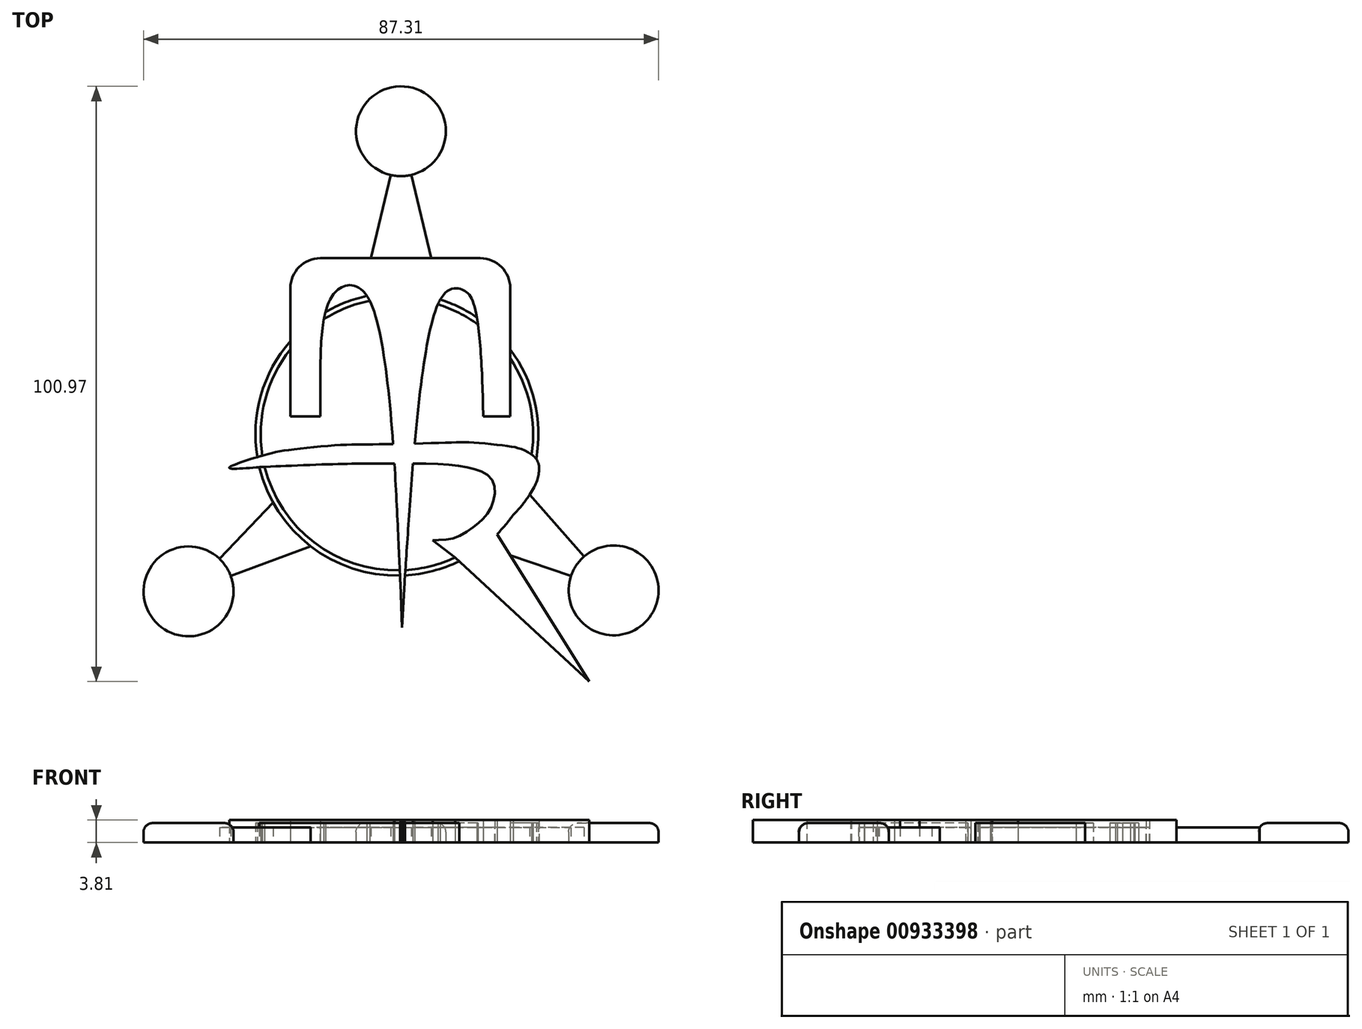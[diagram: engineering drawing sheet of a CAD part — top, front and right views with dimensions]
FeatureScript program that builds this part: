
annotation { "Feature Type Name" : "Feature", "Feature Type Description" : "" }
export const myFeature = defineFeature(function(context is Context, id is Id, definition is map)
    precondition{}
    {
        {
            var Q0;
            Q0=qCreatedBy(makeId("Top.planeOp"),FACE);
            var sketch = newSketch(context, id + "F0", { "sketchPlane" : qUnion([Q0])});
            skCircle(sketch, "E0", {"center": v(-18.12, 70.03) * mm, "radius": 7.62 * mm});
            skCircle(sketch, "E1", {"center": v(17.93, -7.86) * mm, "radius": 7.62 * mm});
            skCircle(sketch, "E2", {"center": v(-54.14, -8.03) * mm, "radius": 7.62 * mm});
            skCircle(sketch, "E3", {"center": v(-18.8, 18.65) * mm, "radius": 23.1 * mm});
            skLineSegment(sketch, "E4", {"start": v(-54.14, -8.03) * mm, "end": v(-39.17, 7.74) * mm});
            skLineSegment(sketch, "E5", {"start": v(-54.14, -8.03) * mm, "end": v(-32.45, 0) * mm});
            skLineSegment(sketch, "E6", {"start": v(-5.15, 0) * mm, "end": v(17.93, -7.86) * mm});
            skLineSegment(sketch, "E7", {"start": v(17.93, -7.86) * mm, "end": v(2.4, 9.9) * mm});
            skLineSegment(sketch, "E8", {"start": v(-18.12, 70.03) * mm, "end": v(-28.3, 26.96) * mm});
            skLineSegment(sketch, "E9", {"start": v(-18.12, 70.03) * mm, "end": v(-11.05, 40.42) * mm});
            skPoint(sketch, "E10.startSnap0", {"position": v(-23.2, 48.5) * mm});
            skLineSegment(sketch, "E11", {"start": v(-36.87, 21.63) * mm, "end": v(-36.87, 48.5) * mm});
            skLineSegment(sketch, "E12", {"start": v(0.4, 21.63) * mm, "end": v(0.4, 48.5) * mm});
            skFitSpline(sketch, "E13", {"points": [v(-31.8, 21.63) * mm, v(-30.76, 39.94) * mm, v(-28.08, 43.6) * mm, v(-23.14, 40.68) * mm, v(-17.9, -9.73) * mm, v(-11.9, 40.58) * mm, v(-7.9, 43.22) * mm, v(-5.88, 41.03) * mm, v(-4.16, 21.63) * mm], "startDerivative": vector(-1.17, 195.1) * mm, "endDerivative": vector(3.47, -161.5) * mm});
            skLineSegment(sketch, "E14", {"start": v(-36.87, 48.5) * mm, "end": v(0.4, 48.5) * mm});
            skLineSegment(sketch, "E15", {"start": v(-17.9, -9.73) * mm, "end": v(-17.9, -14.17) * mm});
            skLineSegment(sketch, "E16", {"start": v(-17.9, -14.17) * mm, "end": v(-17.52, -6.55) * mm});
            skLineSegment(sketch, "E17", {"start": v(-17.52, -6.55) * mm, "end": v(-18.21, -6.73) * mm});
            skLineSegment(sketch, "E18", {"start": v(-18.21, -6.73) * mm, "end": v(-17.9, -14.17) * mm});
            skLineSegment(sketch, "E19", {"start": v(-36.87, 21.63) * mm, "end": v(-31.8, 21.63) * mm});
            skLineSegment(sketch, "E20", {"start": v(-4.16, 21.63) * mm, "end": v(0.4, 21.63) * mm});
            skLineSegment(sketch, "E21", {"start": v(2.4, 9.9) * mm, "end": v(1.54, 10.88) * mm});
            skLineSegment(sketch, "E22", {"start": v(-2.32, 2.44) * mm, "end": v(13.81, -23.32) * mm});
            skLineSegment(sketch, "E23", {"start": v(13.81, -23.32) * mm, "end": v(-8.94, -2.26) * mm});
            skLineSegment(sketch, "E24", {"start": v(-8.94, -2.26) * mm, "end": v(-12.76, 0.66) * mm});
            skFitSpline(sketch, "E25", {"points": [v(-2.32, 2.44) * mm, v(0, 4.2) * mm, v(1.94, 6) * mm, v(4.56, 9.84) * mm, v(5.3, 12.42) * mm, v(4.8, 14.47) * mm, v(2.43, 16.06) * mm, v(0, 16.62) * mm, v(-5.95, 17.23) * mm, v(-10.01, 17.21) * mm, v(-21.72, 16.93) * mm, v(-28.25, 16.82) * mm, v(-37.37, 15.94) * mm, v(-41.62, 15.02) * mm, v(-47.23, 12.94) * mm, v(-42.13, 13.05) * mm, v(-38.06, 13.23) * mm, v(-33.34, 13.44) * mm, v(-29.13, 13.56) * mm, v(-26.22, 13.64) * mm, v(-22.13, 13.65) * mm, v(-14.68, 13.65) * mm, v(-8.81, 13.33) * mm, v(-5.68, 12.71) * mm, v(-3.59, 11.87) * mm, v(-2.32, 10.15) * mm, v(-2.32, 7.85) * mm, v(-3.15, 5.58) * mm, v(-4.58, 3.91) * mm, v(-5.97, 2.8) * mm, v(-8.54, 1.23) * mm, v(-10.7, 0.74) * mm, v(-12.76, 0.66) * mm], "startDerivative": vector(96.56, 70.7) * mm, "endDerivative": vector(-65.55, -2.96) * mm});
            skCircle(sketch, "E26", {"center": v(-18.8, 18.65) * mm, "radius": 24 * mm});
            skSolve(sketch);
        }
        {
            var Q0;
            {var subQ0=sQuery(id+"F0.wireOp",EDGE,"E14");var subQ3=sQuery(id+"F0.wireOp",EDGE,"E8");var subQ4=makeQuery(id+"F0.imprint","INTERSECT",VERTEX,{"derivedFrom":[subQ3,subQ0]});Q0=makeQuery(id+"F0.imprint","IMPRINT",FACE,{"disambiguationData":[TD([[makeQuery(id+"F0.imprint","IMPRINT",EDGE,{"disambiguationData":[TD([[subQ4,-1.0]])],"derivedFrom":subQ3}),-1.0]])]});}
            var Q1;
            {var subQ0=sQuery(id+"F0.wireOp",EDGE,"E13");var subQ1=sQuery(id+"F0.wireOp",EDGE,"E3");var subQ2=makeQuery(id+"F0.imprint","INTERSECT",VERTEX,{"disambiguationData":[OD(3.0)],"derivedFrom":[subQ1,subQ0]});Q1=makeQuery(id+"F0.imprint","IMPRINT",FACE,{"disambiguationData":[TD([[makeQuery(id+"F0.imprint","IMPRINT",EDGE,{"disambiguationData":[TD([[subQ2,-1.0]])],"derivedFrom":subQ1}),-1.0]])]});}
            var Q2;
            {var subQ5=sQuery(id+"F0.wireOp",EDGE,"E19");Q2=makeQuery(id+"F0.imprint","IMPRINT",FACE,{"disambiguationData":[TD([[makeQuery(id+"F0.imprint","IMPRINT",EDGE,{"derivedFrom":subQ5}),1.0]])]});}
            var Q3;
            {var subQ5=sQuery(id+"F0.wireOp",EDGE,"E8");var subQ8=sQuery(id+"F0.wireOp",EDGE,"E14");var subQ10=makeQuery(id+"F0.imprint","INTERSECT",VERTEX,{"derivedFrom":[subQ5,subQ8]});Q3=makeQuery(id+"F0.imprint","IMPRINT",FACE,{"disambiguationData":[TD([[makeQuery(id+"F0.imprint","IMPRINT",EDGE,{"disambiguationData":[TD([[subQ10,-1.0]])],"derivedFrom":subQ5}),1.0]])]});}
            var Q4;
            {var subQ0=sQuery(id+"F0.wireOp",EDGE,"E14");var subQ3=sQuery(id+"F0.wireOp",EDGE,"E9");var subQ4=makeQuery(id+"F0.imprint","INTERSECT",VERTEX,{"derivedFrom":[subQ3,subQ0]});Q4=makeQuery(id+"F0.imprint","IMPRINT",FACE,{"disambiguationData":[TD([[makeQuery(id+"F0.imprint","IMPRINT",EDGE,{"disambiguationData":[TD([[subQ4,-1.0]])],"derivedFrom":subQ3}),1.0]])]});}
            var Q5;
            {var subQ0=sQuery(id+"F0.wireOp",EDGE,"E13");var subQ1=sQuery(id+"F0.wireOp",EDGE,"E3");var subQ2=makeQuery(id+"F0.imprint","INTERSECT",VERTEX,{"disambiguationData":[OD(1.0)],"derivedFrom":[subQ1,subQ0]});Q5=makeQuery(id+"F0.imprint","IMPRINT",FACE,{"disambiguationData":[TD([[makeQuery(id+"F0.imprint","IMPRINT",EDGE,{"disambiguationData":[TD([[subQ2,-1.0]])],"derivedFrom":subQ1}),1.0]])]});}
            var Q6;
            {var subQ0=sQuery(id+"F0.wireOp",EDGE,"E13");var subQ1=sQuery(id+"F0.wireOp",EDGE,"E3");var subQ2=makeQuery(id+"F0.imprint","INTERSECT",VERTEX,{"disambiguationData":[OD(1.0)],"derivedFrom":[subQ1,subQ0]});Q6=makeQuery(id+"F0.imprint","IMPRINT",FACE,{"disambiguationData":[TD([[makeQuery(id+"F0.imprint","IMPRINT",EDGE,{"disambiguationData":[TD([[subQ2,-1.0]])],"derivedFrom":subQ1}),-1.0]])]});}
            var Q7;
            {var subQ0=sQuery(id+"F0.wireOp",EDGE,"E25");var subQ1=sQuery(id+"F0.wireOp",EDGE,"E3");var subQ2=makeQuery(id+"F0.imprint","INTERSECT",VERTEX,{"disambiguationData":[OD(0.0)],"derivedFrom":[subQ1,subQ0]});Q7=makeQuery(id+"F0.imprint","IMPRINT",FACE,{"disambiguationData":[TD([[makeQuery(id+"F0.imprint","IMPRINT",EDGE,{"disambiguationData":[TD([[subQ2,-1.0]])],"derivedFrom":subQ1}),1.0]])]});}
            var Q8;
            {var subQ0=sQuery(id+"F0.wireOp",EDGE,"E26");var subQ1=sQuery(id+"F0.wireOp",EDGE,"E25");var subQ2=makeQuery(id+"F0.imprint","INTERSECT",VERTEX,{"disambiguationData":[OD(1.0)],"derivedFrom":[subQ1,subQ0]});Q8=makeQuery(id+"F0.imprint","IMPRINT",FACE,{"disambiguationData":[TD([[makeQuery(id+"F0.imprint","IMPRINT",EDGE,{"disambiguationData":[TD([[subQ2,-1.0]])],"derivedFrom":subQ1}),1.0]])]});}
            var Q9;
            {var subQ0=sQuery(id+"F0.wireOp",EDGE,"E25");var subQ1=sQuery(id+"F0.wireOp",EDGE,"E3");var subQ2=makeQuery(id+"F0.imprint","INTERSECT",VERTEX,{"disambiguationData":[OD(0.0)],"derivedFrom":[subQ1,subQ0]});Q9=makeQuery(id+"F0.imprint","IMPRINT",FACE,{"disambiguationData":[TD([[makeQuery(id+"F0.imprint","IMPRINT",EDGE,{"disambiguationData":[TD([[subQ2,-1.0]])],"derivedFrom":subQ1}),-1.0]])]});}
            var Q10;
            {var subQ0=sQuery(id+"F0.wireOp",EDGE,"E25");var subQ1=sQuery(id+"F0.wireOp",EDGE,"E13");var subQ2=makeQuery(id+"F0.imprint","INTERSECT",VERTEX,{"disambiguationData":[OD(0.0)],"derivedFrom":[subQ1,subQ0]});Q10=makeQuery(id+"F0.imprint","IMPRINT",FACE,{"disambiguationData":[TD([[makeQuery(id+"F0.imprint","IMPRINT",EDGE,{"disambiguationData":[TD([[subQ2,-1.0]])],"derivedFrom":subQ1}),1.0]])]});}
            var Q11;
            {var subQ0=sQuery(id+"F0.wireOp",EDGE,"E13");var subQ1=sQuery(id+"F0.wireOp",EDGE,"E3");var subQ2=makeQuery(id+"F0.imprint","INTERSECT",VERTEX,{"disambiguationData":[OD(4.0)],"derivedFrom":[subQ1,subQ0]});Q11=makeQuery(id+"F0.imprint","IMPRINT",FACE,{"disambiguationData":[TD([[makeQuery(id+"F0.imprint","IMPRINT",EDGE,{"disambiguationData":[TD([[subQ2,-1.0]])],"derivedFrom":subQ1}),1.0]])]});}
            var Q12;
            {var subQ6=sQuery(id+"F0.wireOp",EDGE,"E24");Q12=makeQuery(id+"F0.imprint","IMPRINT",FACE,{"disambiguationData":[TD([[makeQuery(id+"F0.imprint","IMPRINT",EDGE,{"derivedFrom":subQ6}),-1.0]])]});}
            var Q13;
            {var subQ0=sQuery(id+"F0.wireOp",EDGE,"E6");var subQ1=sQuery(id+"F0.wireOp",EDGE,"E3");var subQ2=makeQuery(id+"F0.imprint","INTERSECT",VERTEX,{"derivedFrom":[subQ1,subQ0]});Q13=makeQuery(id+"F0.imprint","IMPRINT",FACE,{"disambiguationData":[TD([[makeQuery(id+"F0.imprint","IMPRINT",EDGE,{"disambiguationData":[TD([[subQ2,-1.0]])],"derivedFrom":subQ0}),-1.0]])]});}
            var Q14;
            {var subQ0=sQuery(id+"F0.wireOp",EDGE,"E22");var subQ1=sQuery(id+"F0.wireOp",EDGE,"E6");var subQ2=makeQuery(id+"F0.imprint","INTERSECT",VERTEX,{"derivedFrom":[subQ1,subQ0]});Q14=makeQuery(id+"F0.imprint","IMPRINT",FACE,{"disambiguationData":[TD([[makeQuery(id+"F0.imprint","IMPRINT",EDGE,{"disambiguationData":[TD([[subQ2,1.0]])],"derivedFrom":subQ1}),-1.0]])]});}
            var Q15;
            {var subQ0=sQuery(id+"F0.wireOp",EDGE,"E6");var subQ1=sQuery(id+"F0.wireOp",EDGE,"E3");var subQ2=makeQuery(id+"F0.imprint","INTERSECT",VERTEX,{"derivedFrom":[subQ1,subQ0]});Q15=makeQuery(id+"F0.imprint","IMPRINT",FACE,{"disambiguationData":[TD([[makeQuery(id+"F0.imprint","IMPRINT",EDGE,{"disambiguationData":[TD([[subQ2,-1.0]])],"derivedFrom":subQ0}),1.0]])]});}
            var Q16;
            {var subQ0=sQuery(id+"F0.wireOp",EDGE,"E22");var subQ1=sQuery(id+"F0.wireOp",EDGE,"E6");var subQ2=makeQuery(id+"F0.imprint","INTERSECT",VERTEX,{"derivedFrom":[subQ1,subQ0]});Q16=makeQuery(id+"F0.imprint","IMPRINT",FACE,{"disambiguationData":[TD([[makeQuery(id+"F0.imprint","IMPRINT",EDGE,{"disambiguationData":[TD([[subQ2,1.0]])],"derivedFrom":subQ1}),1.0]])]});}
            var Q17;
            {var subQ0=sQuery(id+"F0.wireOp",EDGE,"E7");var subQ1=sQuery(id+"F0.wireOp",EDGE,"E3");var subQ2=makeQuery(id+"F0.imprint","INTERSECT",VERTEX,{"derivedFrom":[subQ1,subQ0]});Q17=makeQuery(id+"F0.imprint","IMPRINT",FACE,{"disambiguationData":[TD([[makeQuery(id+"F0.imprint","IMPRINT",EDGE,{"disambiguationData":[TD([[subQ2,-1.0]])],"derivedFrom":subQ1}),-1.0]])]});}
            var Q18;
            {var subQ0=sQuery(id+"F0.wireOp",EDGE,"E25");var subQ1=sQuery(id+"F0.wireOp",EDGE,"E7");var subQ2=makeQuery(id+"F0.imprint","INTERSECT",VERTEX,{"derivedFrom":[subQ1,subQ0]});Q18=makeQuery(id+"F0.imprint","IMPRINT",FACE,{"disambiguationData":[TD([[makeQuery(id+"F0.imprint","IMPRINT",EDGE,{"disambiguationData":[TD([[subQ2,-1.0]])],"derivedFrom":subQ1}),-1.0]])]});}
            var Q19;
            {var subQ0=sQuery(id+"F0.wireOp",EDGE,"E25");var subQ1=sQuery(id+"F0.wireOp",EDGE,"E7");var subQ2=makeQuery(id+"F0.imprint","INTERSECT",VERTEX,{"derivedFrom":[subQ1,subQ0]});Q19=makeQuery(id+"F0.imprint","IMPRINT",FACE,{"disambiguationData":[TD([[makeQuery(id+"F0.imprint","IMPRINT",EDGE,{"disambiguationData":[TD([[subQ2,-1.0]])],"derivedFrom":subQ1}),1.0]])]});}
            var Q20;
            {var subQ1=sQuery(id+"F0.wireOp",EDGE,"E3");var subQ3=sQuery(id+"F0.wireOp",EDGE,"E7");var subQ4=makeQuery(id+"F0.imprint","INTERSECT",VERTEX,{"derivedFrom":[subQ1,subQ3]});Q20=makeQuery(id+"F0.imprint","IMPRINT",FACE,{"disambiguationData":[TD([[makeQuery(id+"F0.imprint","IMPRINT",EDGE,{"disambiguationData":[TD([[subQ4,1.0]])],"derivedFrom":subQ3}),1.0]])]});}
            var Q21;
            {var subQ1=sQuery(id+"F0.wireOp",EDGE,"E22");var subQ3=sQuery(id+"F0.wireOp",EDGE,"E26");var subQ4=makeQuery(id+"F0.imprint","INTERSECT",VERTEX,{"derivedFrom":[subQ1,subQ3]});Q21=makeQuery(id+"F0.imprint","IMPRINT",FACE,{"disambiguationData":[TD([[makeQuery(id+"F0.imprint","IMPRINT",EDGE,{"disambiguationData":[TD([[subQ4,-1.0]])],"derivedFrom":subQ3}),1.0]])]});}
            var Q22;
            {var subQ0=sQuery(id+"F0.wireOp",EDGE,"E17");Q22=makeQuery(id+"F0.imprint","IMPRINT",FACE,{"disambiguationData":[TD([[makeQuery(id+"F0.imprint","IMPRINT",EDGE,{"derivedFrom":subQ0}),-1.0]])]});}
            var Q23;
            {var subQ0=sQuery(id+"F0.wireOp",EDGE,"E13");var subQ1=sQuery(id+"F0.wireOp",EDGE,"E3");var subQ2=makeQuery(id+"F0.imprint","INTERSECT",VERTEX,{"disambiguationData":[OD(4.0)],"derivedFrom":[subQ1,subQ0]});Q23=makeQuery(id+"F0.imprint","IMPRINT",FACE,{"disambiguationData":[TD([[makeQuery(id+"F0.imprint","IMPRINT",EDGE,{"disambiguationData":[TD([[subQ2,-1.0]])],"derivedFrom":subQ1}),-1.0]])]});}
            var Q24;
            {var subQ2=sQuery(id+"F0.wireOp",EDGE,"E17");Q24=makeQuery(id+"F0.imprint","IMPRINT",FACE,{"disambiguationData":[TD([[makeQuery(id+"F0.imprint","IMPRINT",EDGE,{"derivedFrom":subQ2}),1.0]])]});}
            var Q25;
            {var subQ0=sQuery(id+"F0.wireOp",EDGE,"E15");Q25=makeQuery(id+"F0.imprint","IMPRINT",FACE,{"disambiguationData":[TD([[makeQuery(id+"F0.imprint","IMPRINT",EDGE,{"derivedFrom":subQ0}),1.0]])]});}
            var Q26;
            {var subQ0=sQuery(id+"F0.wireOp",EDGE,"E15");Q26=makeQuery(id+"F0.imprint","IMPRINT",FACE,{"disambiguationData":[TD([[makeQuery(id+"F0.imprint","IMPRINT",EDGE,{"derivedFrom":subQ0}),-1.0]])]});}
            var Q27;
            {var subQ0=sQuery(id+"F0.wireOp",EDGE,"E13");var subQ1=sQuery(id+"F0.wireOp",EDGE,"E3");var subQ2=makeQuery(id+"F0.imprint","INTERSECT",VERTEX,{"disambiguationData":[OD(0.0)],"derivedFrom":[subQ1,subQ0]});Q27=makeQuery(id+"F0.imprint","IMPRINT",FACE,{"disambiguationData":[TD([[makeQuery(id+"F0.imprint","IMPRINT",EDGE,{"disambiguationData":[TD([[subQ2,1.0]])],"derivedFrom":subQ1}),-1.0]])]});}
            var Q28;
            {var subQ5=sQuery(id+"F0.wireOp",EDGE,"E20");Q28=makeQuery(id+"F0.imprint","IMPRINT",FACE,{"disambiguationData":[TD([[makeQuery(id+"F0.imprint","IMPRINT",EDGE,{"derivedFrom":subQ5}),1.0]])]});}
            extrude(context, id + "F1", {"entities" : qUnion([Q0, Q1, Q2, Q3, Q4, Q5, Q6, Q7, Q8, Q9, Q10, Q11, Q12, Q13, Q14, Q15, Q16, Q17, Q18, Q19, Q20, Q21, Q22, Q23, Q24, Q25, Q26, Q27, Q28]), "depth" : 3.8 * mm, "offsetDistance" : 25.4 * mm});
        }
        {
            var Q0;
            {var subQ3=sQuery(id+"F0.wireOp",EDGE,"E13");var subQ5=sQuery(id+"F0.wireOp",EDGE,"E26");var subQ6=makeQuery(id+"F0.imprint","INTERSECT",VERTEX,{"disambiguationData":[OD(1.0)],"derivedFrom":[subQ3,subQ5]});Q0=makeQuery(id+"F0.imprint","IMPRINT",FACE,{"disambiguationData":[TD([[makeQuery(id+"F0.imprint","IMPRINT",EDGE,{"disambiguationData":[TD([[subQ6,-1.0]])],"derivedFrom":subQ3}),-1.0]])]});}
            var Q1;
            {var subQ0=sQuery(id+"F0.wireOp",EDGE,"E5");var subQ1=sQuery(id+"F0.wireOp",EDGE,"E3");var subQ2=makeQuery(id+"F0.imprint","INTERSECT",VERTEX,{"derivedFrom":[subQ1,subQ0]});Q1=makeQuery(id+"F0.imprint","IMPRINT",FACE,{"disambiguationData":[TD([[makeQuery(id+"F0.imprint","IMPRINT",EDGE,{"disambiguationData":[TD([[subQ2,-1.0]])],"derivedFrom":subQ1}),-1.0]])]});}
            var Q2;
            {var subQ0=sQuery(id+"F0.wireOp",EDGE,"E4");var subQ1=sQuery(id+"F0.wireOp",EDGE,"E3");var subQ2=makeQuery(id+"F0.imprint","INTERSECT",VERTEX,{"derivedFrom":[subQ1,subQ0]});Q2=makeQuery(id+"F0.imprint","IMPRINT",FACE,{"disambiguationData":[TD([[makeQuery(id+"F0.imprint","IMPRINT",EDGE,{"disambiguationData":[TD([[subQ2,-1.0]])],"derivedFrom":subQ1}),-1.0]])]});}
            var Q3;
            {var subQ0=sQuery(id+"F0.wireOp",EDGE,"E4");var subQ1=sQuery(id+"F0.wireOp",EDGE,"E3");var subQ2=makeQuery(id+"F0.imprint","INTERSECT",VERTEX,{"derivedFrom":[subQ1,subQ0]});Q3=makeQuery(id+"F0.imprint","IMPRINT",FACE,{"disambiguationData":[TD([[makeQuery(id+"F0.imprint","IMPRINT",EDGE,{"disambiguationData":[TD([[subQ2,1.0]])],"derivedFrom":subQ1}),-1.0]])]});}
            var Q4;
            {var subQ0=sQuery(id+"F0.wireOp",EDGE,"E11");var subQ1=sQuery(id+"F0.wireOp",EDGE,"E3");var subQ2=makeQuery(id+"F0.imprint","INTERSECT",VERTEX,{"derivedFrom":[subQ1,subQ0]});Q4=makeQuery(id+"F0.imprint","IMPRINT",FACE,{"disambiguationData":[TD([[makeQuery(id+"F0.imprint","IMPRINT",EDGE,{"disambiguationData":[TD([[subQ2,-1.0]])],"derivedFrom":subQ1}),-1.0]])]});}
            var Q5;
            {var subQ1=sQuery(id+"F0.wireOp",EDGE,"E22");var subQ3=sQuery(id+"F0.wireOp",EDGE,"E26");var subQ4=makeQuery(id+"F0.imprint","INTERSECT",VERTEX,{"derivedFrom":[subQ1,subQ3]});Q5=makeQuery(id+"F0.imprint","IMPRINT",FACE,{"disambiguationData":[TD([[makeQuery(id+"F0.imprint","IMPRINT",EDGE,{"disambiguationData":[TD([[subQ4,-1.0]])],"derivedFrom":subQ3}),1.0]])]});}
            var Q6;
            {var subQ0=sQuery(id+"F0.wireOp",EDGE,"E12");var subQ1=sQuery(id+"F0.wireOp",EDGE,"E3");var subQ2=makeQuery(id+"F0.imprint","INTERSECT",VERTEX,{"derivedFrom":[subQ1,subQ0]});Q6=makeQuery(id+"F0.imprint","IMPRINT",FACE,{"disambiguationData":[TD([[makeQuery(id+"F0.imprint","IMPRINT",EDGE,{"disambiguationData":[TD([[subQ2,1.0]])],"derivedFrom":subQ1}),-1.0]])]});}
            var Q7;
            {var subQ0=sQuery(id+"F0.wireOp",EDGE,"E9");var subQ1=sQuery(id+"F0.wireOp",EDGE,"E3");var subQ2=makeQuery(id+"F0.imprint","INTERSECT",VERTEX,{"derivedFrom":[subQ1,subQ0]});Q7=makeQuery(id+"F0.imprint","IMPRINT",FACE,{"disambiguationData":[TD([[makeQuery(id+"F0.imprint","IMPRINT",EDGE,{"disambiguationData":[TD([[subQ2,1.0]])],"derivedFrom":subQ1}),-1.0]])]});}
            var Q8;
            {var subQ0=sQuery(id+"F0.wireOp",EDGE,"E9");var subQ1=sQuery(id+"F0.wireOp",EDGE,"E3");var subQ2=makeQuery(id+"F0.imprint","INTERSECT",VERTEX,{"derivedFrom":[subQ1,subQ0]});Q8=makeQuery(id+"F0.imprint","IMPRINT",FACE,{"disambiguationData":[TD([[makeQuery(id+"F0.imprint","IMPRINT",EDGE,{"disambiguationData":[TD([[subQ2,-1.0]])],"derivedFrom":subQ1}),-1.0]])]});}
            var Q9;
            {var subQ0=sQuery(id+"F0.wireOp",EDGE,"E8");var subQ1=sQuery(id+"F0.wireOp",EDGE,"E3");var subQ2=makeQuery(id+"F0.imprint","INTERSECT",VERTEX,{"derivedFrom":[subQ1,subQ0]});Q9=makeQuery(id+"F0.imprint","IMPRINT",FACE,{"disambiguationData":[TD([[makeQuery(id+"F0.imprint","IMPRINT",EDGE,{"disambiguationData":[TD([[subQ2,1.0]])],"derivedFrom":subQ1}),-1.0]])]});}
            var Q10;
            {var subQ0=sQuery(id+"F0.wireOp",EDGE,"E8");var subQ1=sQuery(id+"F0.wireOp",EDGE,"E3");var subQ2=makeQuery(id+"F0.imprint","INTERSECT",VERTEX,{"derivedFrom":[subQ1,subQ0]});Q10=makeQuery(id+"F0.imprint","IMPRINT",FACE,{"disambiguationData":[TD([[makeQuery(id+"F0.imprint","IMPRINT",EDGE,{"disambiguationData":[TD([[subQ2,-1.0]])],"derivedFrom":subQ1}),-1.0]])]});}
            var Q11;
            {var subQ0=sQuery(id+"F0.wireOp",EDGE,"E8");var subQ1=sQuery(id+"F0.wireOp",EDGE,"E0");var subQ2=makeQuery(id+"F0.imprint","INTERSECT",VERTEX,{"derivedFrom":[subQ1,subQ0]});Q11=makeQuery(id+"F0.imprint","IMPRINT",FACE,{"disambiguationData":[TD([[makeQuery(id+"F0.imprint","IMPRINT",EDGE,{"disambiguationData":[TD([[subQ2,1.0]])],"derivedFrom":subQ1}),1.0]])]});}
            var Q12;
            {var subQ0=sQuery(id+"F0.wireOp",EDGE,"E8");var subQ1=sQuery(id+"F0.wireOp",EDGE,"E0");var subQ2=makeQuery(id+"F0.imprint","INTERSECT",VERTEX,{"derivedFrom":[subQ1,subQ0]});Q12=makeQuery(id+"F0.imprint","IMPRINT",FACE,{"disambiguationData":[TD([[makeQuery(id+"F0.imprint","IMPRINT",EDGE,{"disambiguationData":[TD([[subQ2,-1.0]])],"derivedFrom":subQ1}),1.0]])]});}
            var Q13;
            {var subQ0=sQuery(id+"F0.wireOp",EDGE,"E4");var subQ1=sQuery(id+"F0.wireOp",EDGE,"E2");var subQ2=makeQuery(id+"F0.imprint","INTERSECT",VERTEX,{"derivedFrom":[subQ1,subQ0]});Q13=makeQuery(id+"F0.imprint","IMPRINT",FACE,{"disambiguationData":[TD([[makeQuery(id+"F0.imprint","IMPRINT",EDGE,{"disambiguationData":[TD([[subQ2,-1.0]])],"derivedFrom":subQ1}),1.0]])]});}
            var Q14;
            {var subQ0=sQuery(id+"F0.wireOp",EDGE,"E4");var subQ1=sQuery(id+"F0.wireOp",EDGE,"E2");var subQ2=makeQuery(id+"F0.imprint","INTERSECT",VERTEX,{"derivedFrom":[subQ1,subQ0]});Q14=makeQuery(id+"F0.imprint","IMPRINT",FACE,{"disambiguationData":[TD([[makeQuery(id+"F0.imprint","IMPRINT",EDGE,{"disambiguationData":[TD([[subQ2,1.0]])],"derivedFrom":subQ1}),1.0]])]});}
            var Q15;
            {var subQ0=sQuery(id+"F0.wireOp",EDGE,"E6");var subQ1=sQuery(id+"F0.wireOp",EDGE,"E1");var subQ2=makeQuery(id+"F0.imprint","INTERSECT",VERTEX,{"derivedFrom":[subQ1,subQ0]});Q15=makeQuery(id+"F0.imprint","IMPRINT",FACE,{"disambiguationData":[TD([[makeQuery(id+"F0.imprint","IMPRINT",EDGE,{"disambiguationData":[TD([[subQ2,-1.0]])],"derivedFrom":subQ1}),1.0]])]});}
            var Q16;
            {var subQ0=sQuery(id+"F0.wireOp",EDGE,"E6");var subQ1=sQuery(id+"F0.wireOp",EDGE,"E1");var subQ2=makeQuery(id+"F0.imprint","INTERSECT",VERTEX,{"derivedFrom":[subQ1,subQ0]});Q16=makeQuery(id+"F0.imprint","IMPRINT",FACE,{"disambiguationData":[TD([[makeQuery(id+"F0.imprint","IMPRINT",EDGE,{"disambiguationData":[TD([[subQ2,1.0]])],"derivedFrom":subQ1}),1.0]])]});}
            extrude(context, id + "F2", {"entities" : qUnion([Q0, Q1, Q2, Q3, Q4, Q5, Q6, Q7, Q8, Q9, Q10, Q11, Q12, Q13, Q14, Q15, Q16]), "operationType" : NewBodyOperationType.ADD, "depth" : 3.3 * mm, "offsetDistance" : 25.4 * mm});
        }
        {
            var Q0;
            {var subQ0=sQuery(id+"F0.wireOp",EDGE,"E4");var subQ1=sQuery(id+"F0.wireOp",EDGE,"E2");var subQ2=makeQuery(id+"F0.imprint","INTERSECT",VERTEX,{"derivedFrom":[subQ1,subQ0]});Q0=makeQuery(id+"F0.imprint","IMPRINT",FACE,{"disambiguationData":[TD([[makeQuery(id+"F0.imprint","IMPRINT",EDGE,{"disambiguationData":[TD([[subQ2,1.0]])],"derivedFrom":subQ1}),-1.0]])]});}
            var Q1;
            {var subQ1=sQuery(id+"F0.wireOp",EDGE,"E3");var subQ6=makeQuery(id+"F0.imprint","INTERSECT",VERTEX,{"derivedFrom":[subQ1,sQuery(id+"F0.wireOp",EDGE,"E4")]});Q1=makeQuery(id+"F0.imprint","IMPRINT",FACE,{"disambiguationData":[TD([[makeQuery(id+"F0.imprint","IMPRINT",EDGE,{"disambiguationData":[TD([[subQ6,1.0]])],"derivedFrom":subQ1}),1.0]])]});}
            var Q2;
            {var subQ0=sQuery(id+"F0.wireOp",EDGE,"E19");Q2=makeQuery(id+"F0.imprint","IMPRINT",FACE,{"disambiguationData":[TD([[makeQuery(id+"F0.imprint","IMPRINT",EDGE,{"derivedFrom":subQ0}),-1.0]])]});}
            var Q3;
            {var subQ8=sQuery(id+"F0.wireOp",EDGE,"E20");Q3=makeQuery(id+"F0.imprint","IMPRINT",FACE,{"disambiguationData":[TD([[makeQuery(id+"F0.imprint","IMPRINT",EDGE,{"derivedFrom":subQ8}),-1.0]])]});}
            var Q4;
            {var subQ0=sQuery(id+"F0.wireOp",EDGE,"E24");Q4=makeQuery(id+"F0.imprint","IMPRINT",FACE,{"disambiguationData":[TD([[makeQuery(id+"F0.imprint","IMPRINT",EDGE,{"derivedFrom":subQ0}),1.0]])]});}
            var Q5;
            {var subQ1=sQuery(id+"F0.wireOp",EDGE,"E1");var subQ5=sQuery(id+"F0.wireOp",EDGE,"E6");var subQ6=makeQuery(id+"F0.imprint","INTERSECT",VERTEX,{"derivedFrom":[subQ1,subQ5]});Q5=makeQuery(id+"F0.imprint","IMPRINT",FACE,{"disambiguationData":[TD([[makeQuery(id+"F0.imprint","IMPRINT",EDGE,{"disambiguationData":[TD([[subQ6,1.0]])],"derivedFrom":subQ1}),-1.0]])]});}
            var Q6;
            {var subQ0=sQuery(id+"F0.wireOp",EDGE,"E13");var subQ1=sQuery(id+"F0.wireOp",EDGE,"E9");var subQ2=makeQuery(id+"F0.imprint","INTERSECT",VERTEX,{"derivedFrom":[subQ1,subQ0]});Q6=makeQuery(id+"F0.imprint","IMPRINT",FACE,{"disambiguationData":[TD([[makeQuery(id+"F0.imprint","IMPRINT",EDGE,{"disambiguationData":[TD([[subQ2,-1.0]])],"derivedFrom":subQ1}),1.0]])]});}
            var Q7;
            {var subQ0=sQuery(id+"F0.wireOp",EDGE,"E13");var subQ1=sQuery(id+"F0.wireOp",EDGE,"E8");var subQ2=makeQuery(id+"F0.imprint","INTERSECT",VERTEX,{"derivedFrom":[subQ1,subQ0]});Q7=makeQuery(id+"F0.imprint","IMPRINT",FACE,{"disambiguationData":[TD([[makeQuery(id+"F0.imprint","IMPRINT",EDGE,{"disambiguationData":[TD([[subQ2,-1.0]])],"derivedFrom":subQ1}),-1.0]])]});}
            var Q8;
            {var subQ0=sQuery(id+"F0.wireOp",EDGE,"E13");var subQ1=sQuery(id+"F0.wireOp",EDGE,"E8");var subQ2=makeQuery(id+"F0.imprint","INTERSECT",VERTEX,{"derivedFrom":[subQ1,subQ0]});Q8=makeQuery(id+"F0.imprint","IMPRINT",FACE,{"disambiguationData":[TD([[makeQuery(id+"F0.imprint","IMPRINT",EDGE,{"disambiguationData":[TD([[subQ2,-1.0]])],"derivedFrom":subQ1}),1.0]])]});}
            var Q9;
            {var subQ0=sQuery(id+"F0.wireOp",EDGE,"E8");var subQ1=sQuery(id+"F0.wireOp",EDGE,"E0");var subQ2=makeQuery(id+"F0.imprint","INTERSECT",VERTEX,{"derivedFrom":[subQ1,subQ0]});Q9=makeQuery(id+"F0.imprint","IMPRINT",FACE,{"disambiguationData":[TD([[makeQuery(id+"F0.imprint","IMPRINT",EDGE,{"disambiguationData":[TD([[subQ2,-1.0]])],"derivedFrom":subQ1}),-1.0]])]});}
            var Q10;
            {var subQ0=sQuery(id+"F0.wireOp",EDGE,"E13");var subQ1=sQuery(id+"F0.wireOp",EDGE,"E9");var subQ2=makeQuery(id+"F0.imprint","INTERSECT",VERTEX,{"derivedFrom":[subQ1,subQ0]});Q10=makeQuery(id+"F0.imprint","IMPRINT",FACE,{"disambiguationData":[TD([[makeQuery(id+"F0.imprint","IMPRINT",EDGE,{"disambiguationData":[TD([[subQ2,-1.0]])],"derivedFrom":subQ1}),-1.0]])]});}
            extrude(context, id + "F3", {"entities" : qUnion([Q0, Q1, Q2, Q3, Q4, Q5, Q6, Q7, Q8, Q9, Q10]), "depth" : 2.54 * mm, "offsetDistance" : 25.4 * mm});
        }
        {
            var Q0;
            Q0=makeQuery(id+"F1.opExtrude","SWEPT_EDGE",EDGE,{"disambiguationData":[OSD([sQuery(id+"F0.wireOp",EDGE,"E12"),sQuery(id+"F0.wireOp",EDGE,"E14")])]});
            var Q1;
            Q1=makeQuery(id+"F1.opExtrude","SWEPT_EDGE",EDGE,{"disambiguationData":[OSD([sQuery(id+"F0.wireOp",EDGE,"E11"),sQuery(id+"F0.wireOp",EDGE,"E14")])]});
            fillet(context, id + "F4", {"entities" : qUnion([Q0, Q1]), "tangentPropagation" : true, "radius" : 5.08 * mm, "defaultsChanged" : false, "vertexSettings" : [], "allowEdgeOverflow" : false});
        }
        {
            var Q0;
            Q0=makeQuery(id+"F2.opExtrude","CAP_EDGE",EDGE,{"disambiguationData":[OSD([sQuery(id+"F0.wireOp",EDGE,"E0")])],"isStart":false});
            var Q1;
            Q1=makeQuery(id+"F2.opExtrude","CAP_EDGE",EDGE,{"disambiguationData":[OSD([sQuery(id+"F0.wireOp",EDGE,"E1")])],"isStart":false});
            var Q2;
            Q2=makeQuery(id+"F2.opExtrude","CAP_EDGE",EDGE,{"disambiguationData":[OSD([sQuery(id+"F0.wireOp",EDGE,"E2")])],"isStart":false});
            fillet(context, id + "F5", {"entities" : qUnion([Q0, Q1, Q2]), "tangentPropagation" : true, "radius" : 1.52 * mm, "defaultsChanged" : true, "vertexSettings" : [], "allowEdgeOverflow" : false});
        }
    });
